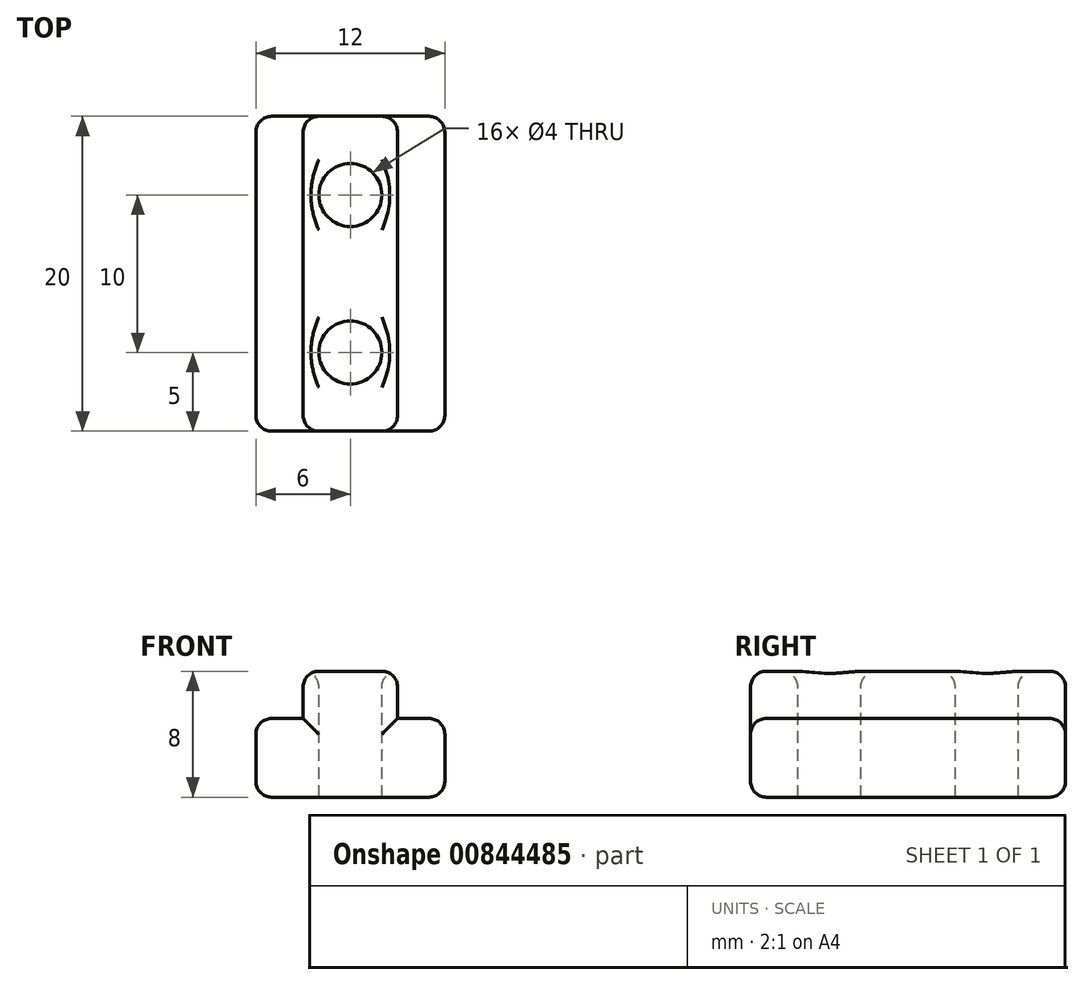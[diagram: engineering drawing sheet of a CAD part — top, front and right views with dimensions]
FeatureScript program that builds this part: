
annotation { "Feature Type Name" : "Feature", "Feature Type Description" : "" }
export const myFeature = defineFeature(function(context is Context, id is Id, definition is map)
    precondition{}
    {
        {
            var Q0;
            Q0=qCreatedBy(makeId("Front.planeOp"),FACE);
            var sketch = newSketch(context, id + "F0", { "sketchPlane" : qUnion([Q0])});
            skLineSegment(sketch, "E0", {"start": v(0, 0) * mm, "end": v(12, 0) * mm});
            skLineSegment(sketch, "E1", {"start": v(12, 0) * mm, "end": v(12, 5) * mm});
            skLineSegment(sketch, "E2", {"start": v(12, 5) * mm, "end": v(9, 5) * mm});
            skLineSegment(sketch, "E3", {"start": v(9, 5) * mm, "end": v(9, 8) * mm});
            skLineSegment(sketch, "E4", {"start": v(9, 8) * mm, "end": v(3, 8) * mm});
            skLineSegment(sketch, "E5", {"start": v(3, 8) * mm, "end": v(3, 5) * mm});
            skLineSegment(sketch, "E6", {"start": v(3, 5) * mm, "end": v(0, 5) * mm});
            skLineSegment(sketch, "E7", {"start": v(0, 5) * mm, "end": v(0, 0) * mm});
            skSolve(sketch);
        }
        {
            var Q0;
            Q0=makeQuery(id+"F0.imprint","IMPRINT",FACE,{"disambiguationData":[TD([[makeQuery(id+"F0.imprint","IMPRINT",EDGE,{"derivedFrom":sQuery(id+"F0.wireOp",EDGE,"E0")}),1.0]])]});
            extrude(context, id + "F1", {"entities" : qUnion([Q0]), "depth" : 20 * mm, "offsetDistance" : 25 * mm});
        }
        {
            var Q0;
            Q0=makeQuery(id+"F1.opExtrude","SWEPT_FACE",FACE,{"disambiguationData":[OSD([sQuery(id+"F0.wireOp",EDGE,"E4")])]});
            var sketch = newSketch(context, id + "F2", { "sketchPlane" : qUnion([Q0])});
            skLineSegment(sketch, "E8", {"start": v(6, -20) * mm, "end": v(6, 0) * mm, "construction": true});
            skCircle(sketch, "E9", {"center": v(6, -5) * mm, "radius": 2 * mm});
            skCircle(sketch, "E10", {"center": v(6, -15) * mm, "radius": 2 * mm});
            skSolve(sketch);
        }
        {
            var Q0;
            Q0=makeQuery(id+"F2.imprint","IMPRINT",FACE,{"disambiguationData":[TD([[makeQuery(id+"F2.imprint","IMPRINT",EDGE,{"derivedFrom":sQuery(id+"F2.wireOp",EDGE,"E9")}),1.0]])]});
            var Q1;
            Q1=makeQuery(id+"F2.imprint","IMPRINT",FACE,{"disambiguationData":[TD([[makeQuery(id+"F2.imprint","IMPRINT",EDGE,{"derivedFrom":sQuery(id+"F2.wireOp",EDGE,"E10")}),1.0]])]});
            extrude(context, id + "F3", {"entities" : qUnion([Q0, Q1]), "operationType" : NewBodyOperationType.REMOVE, "endBound" : BoundingType.THROUGH_ALL, "oppositeDirection" : true, "depth" : 25 * mm, "offsetDistance" : 25 * mm});
        }
        {
            var Q0;
            Q0=makeQuery(id+"F1.opExtrude","SWEPT_FACE",FACE,{"disambiguationData":[OSD([sQuery(id+"F0.wireOp",EDGE,"E4")])]});
            var Q1;
            Q1=makeQuery(id+"F1.opExtrude","SWEPT_FACE",FACE,{"disambiguationData":[OSD([sQuery(id+"F0.wireOp",EDGE,"E1")])]});
            var Q2;
            Q2=makeQuery(id+"F1.opExtrude","SWEPT_FACE",FACE,{"disambiguationData":[OSD([sQuery(id+"F0.wireOp",EDGE,"E7")])]});
            var Q3;
            Q3=makeQuery(id+"F1.opExtrude","CAP_FACE",FACE,{"disambiguationData":[OSD([sQuery(id+"F0.wireOp",EDGE,"E0"),sQuery(id+"F0.wireOp",EDGE,"E1"),sQuery(id+"F0.wireOp",EDGE,"E2"),sQuery(id+"F0.wireOp",EDGE,"E3"),sQuery(id+"F0.wireOp",EDGE,"E4"),sQuery(id+"F0.wireOp",EDGE,"E5"),sQuery(id+"F0.wireOp",EDGE,"E6"),sQuery(id+"F0.wireOp",EDGE,"E7")])],"isStart":false});
            var Q4;
            Q4=makeQuery(id+"F1.opExtrude","CAP_FACE",FACE,{"disambiguationData":[OSD([sQuery(id+"F0.wireOp",EDGE,"E0"),sQuery(id+"F0.wireOp",EDGE,"E1"),sQuery(id+"F0.wireOp",EDGE,"E2"),sQuery(id+"F0.wireOp",EDGE,"E3"),sQuery(id+"F0.wireOp",EDGE,"E4"),sQuery(id+"F0.wireOp",EDGE,"E5"),sQuery(id+"F0.wireOp",EDGE,"E6"),sQuery(id+"F0.wireOp",EDGE,"E7")])],"isStart":true});
            fillet(context, id + "F4", {"entities" : qUnion([Q0, Q1, Q2, Q3, Q4]), "radius" : 1 * mm, "tangentPropagation" : true, "allowEdgeOverflow" : false});
        }
    });
